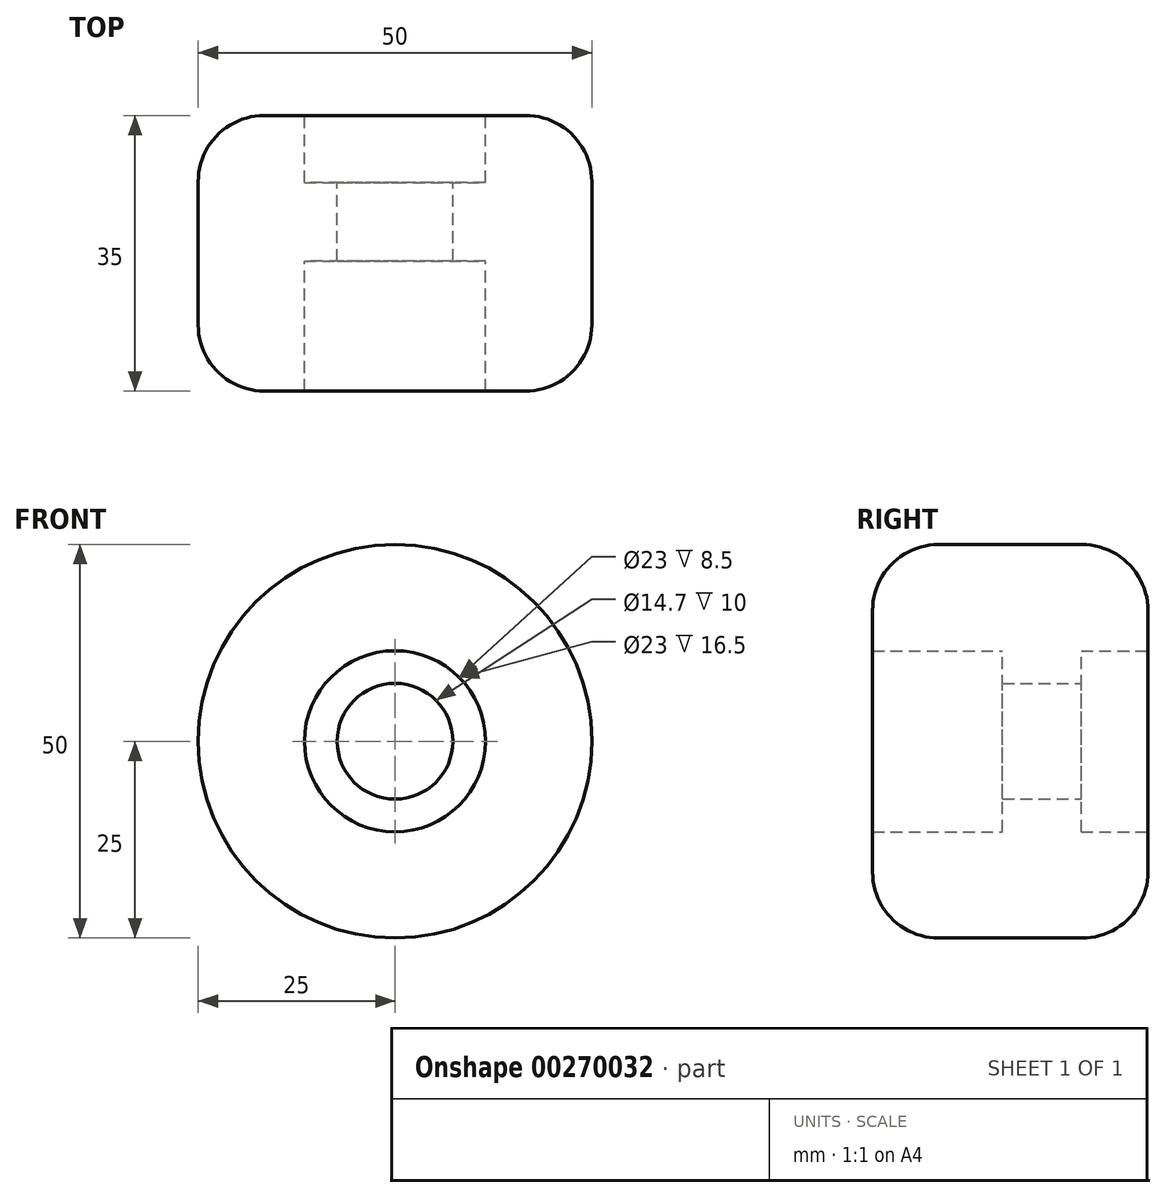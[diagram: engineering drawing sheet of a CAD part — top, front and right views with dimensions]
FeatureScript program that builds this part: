
annotation { "Feature Type Name" : "Feature", "Feature Type Description" : "" }
export const myFeature = defineFeature(function(context is Context, id is Id, definition is map)
    precondition{}
    {
        {
            var Q0;
            Q0=qCreatedBy(makeId("Front.planeOp"),FACE);
            var sketch = newSketch(context, id + "F0", { "sketchPlane" : qUnion([Q0])});
            skCircle(sketch, "E0", {"center": v(0, 0) * mm, "radius": 25 * mm});
            skCircle(sketch, "E1", {"center": v(0, 0) * mm, "radius": 7.35 * mm});
            skCircle(sketch, "E2", {"center": v(0, 0) * mm, "radius": 11.5 * mm});
            skSolve(sketch);
        }
        {
            var Q0;
            Q0=makeQuery(id+"F0.imprint","IMPRINT",FACE,{"disambiguationData":[TD([[makeQuery(id+"F0.imprint","IMPRINT",EDGE,{"derivedFrom":sQuery(id+"F0.wireOp",EDGE,"E0")}),1.0]])]});
            extrude(context, id + "F1", {"entities" : qUnion([Q0]), "depth" : 17.5 * mm, "offsetDistance" : 25 * mm, "hasSecondDirection" : true, "secondDirectionOppositeDirection" : true, "secondDirectionDepth" : 17.5 * mm});
        }
        {
            var Q0;
            Q0=makeQuery(id+"F0.imprint","IMPRINT",FACE,{"disambiguationData":[TD([[makeQuery(id+"F0.imprint","IMPRINT",EDGE,{"derivedFrom":sQuery(id+"F0.wireOp",EDGE,"E1")}),-1.0]])]});
            extrude(context, id + "F2", {"entities" : qUnion([Q0]), "operationType" : NewBodyOperationType.ADD, "depth" : 6 * mm, "offsetDistance" : 25 * mm});
        }
        {
            var Q0;
            Q0=makeQuery(id+"F0.imprint","IMPRINT",FACE,{"disambiguationData":[TD([[makeQuery(id+"F0.imprint","IMPRINT",EDGE,{"derivedFrom":sQuery(id+"F0.wireOp",EDGE,"E1")}),-1.0]])]});
            extrude(context, id + "F3", {"entities" : qUnion([Q0]), "operationType" : NewBodyOperationType.ADD, "oppositeDirection" : true, "depth" : 6 * mm, "offsetDistance" : 25 * mm});
        }
        {
            var Q0;
            Q0=makeQuery(id+"F1.opExtrude","CAP_EDGE",EDGE,{"disambiguationData":[OSD([sQuery(id+"F0.wireOp",EDGE,"E0")])],"isStart":false});
            var Q1;
            Q1=makeQuery(id+"F1.opExtrude","CAP_EDGE",EDGE,{"disambiguationData":[OSD([sQuery(id+"F0.wireOp",EDGE,"E0")])],"isStart":true});
            fillet(context, id + "F4", {"entities" : qUnion([Q0, Q1]), "radius" : 8.4 * mm, "tangentPropagation" : true, "allowEdgeOverflow" : false});
        }
        {
            var Q0;
            Q0=qCreatedBy(makeId("Top.planeOp"),FACE);
            var sketch = newSketch(context, id + "F5", { "sketchPlane" : qUnion([Q0])});
            skLineSegment(sketch, "E3.0", {"start": v(11.5, 0) * mm, "end": v(-11.5, 0) * mm});
            skLineSegment(sketch, "E4", {"start": v(25, 9.53) * mm, "end": v(25, -9.53) * mm});
            skLineSegment(sketch, "E5", {"start": v(-25, -9.53) * mm, "end": v(-25, 9.53) * mm});
            skSolve(sketch);
        }
        {
            var Q0;
            Q0=makeQuery(id+"F2.opExtrude","CAP_FACE",FACE,{"disambiguationData":[OSD([sQuery(id+"F0.wireOp",EDGE,"E1"),sQuery(id+"F0.wireOp",EDGE,"E2")])],"isStart":false});
            extrude(context, id + "F6", {"entities" : qUnion([Q0]), "operationType" : NewBodyOperationType.REMOVE, "oppositeDirection" : true, "depth" : 5 * mm, "offsetDistance" : 25 * mm});
        }
        {
            var Q0;
            Q0=makeQuery(id+"F3.opExtrude","CAP_FACE",FACE,{"disambiguationData":[OSD([sQuery(id+"F0.wireOp",EDGE,"E1"),sQuery(id+"F0.wireOp",EDGE,"E2")])],"isStart":false});
            extrude(context, id + "F7", {"entities" : qUnion([Q0]), "operationType" : NewBodyOperationType.ADD, "depth" : 3 * mm, "offsetDistance" : 25 * mm});
        }
    });
